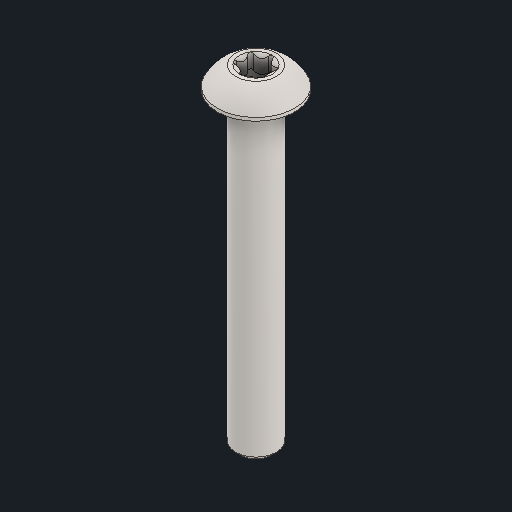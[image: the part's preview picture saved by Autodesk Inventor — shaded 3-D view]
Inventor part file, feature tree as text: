
AUTODESK INVENTOR PART (.ipt)
format: ipt  version: 2024 (Build 280153000, 153)  size: 160,256 bytes
history: native  units: in
note: dims shown in document units (in); Inventor stores cm internally (conversion verified against a paired STEP export)
features: chamfer x1
ambient origin geometry x8: Origin, YZ Plane, XZ Plane, XY Plane, X Axis, Y Axis, Z Axis, Center Point
bodies: Solid1 (feature_tree)
feature tree (1):
  chamfer  "Chamfer2"  [1 undecoded]
note: 1 required parameter value undecoded (feature->parameter linkage not recoverable at this tier; creation-order binding heuristic only, values carry confidence <= 0.55)
